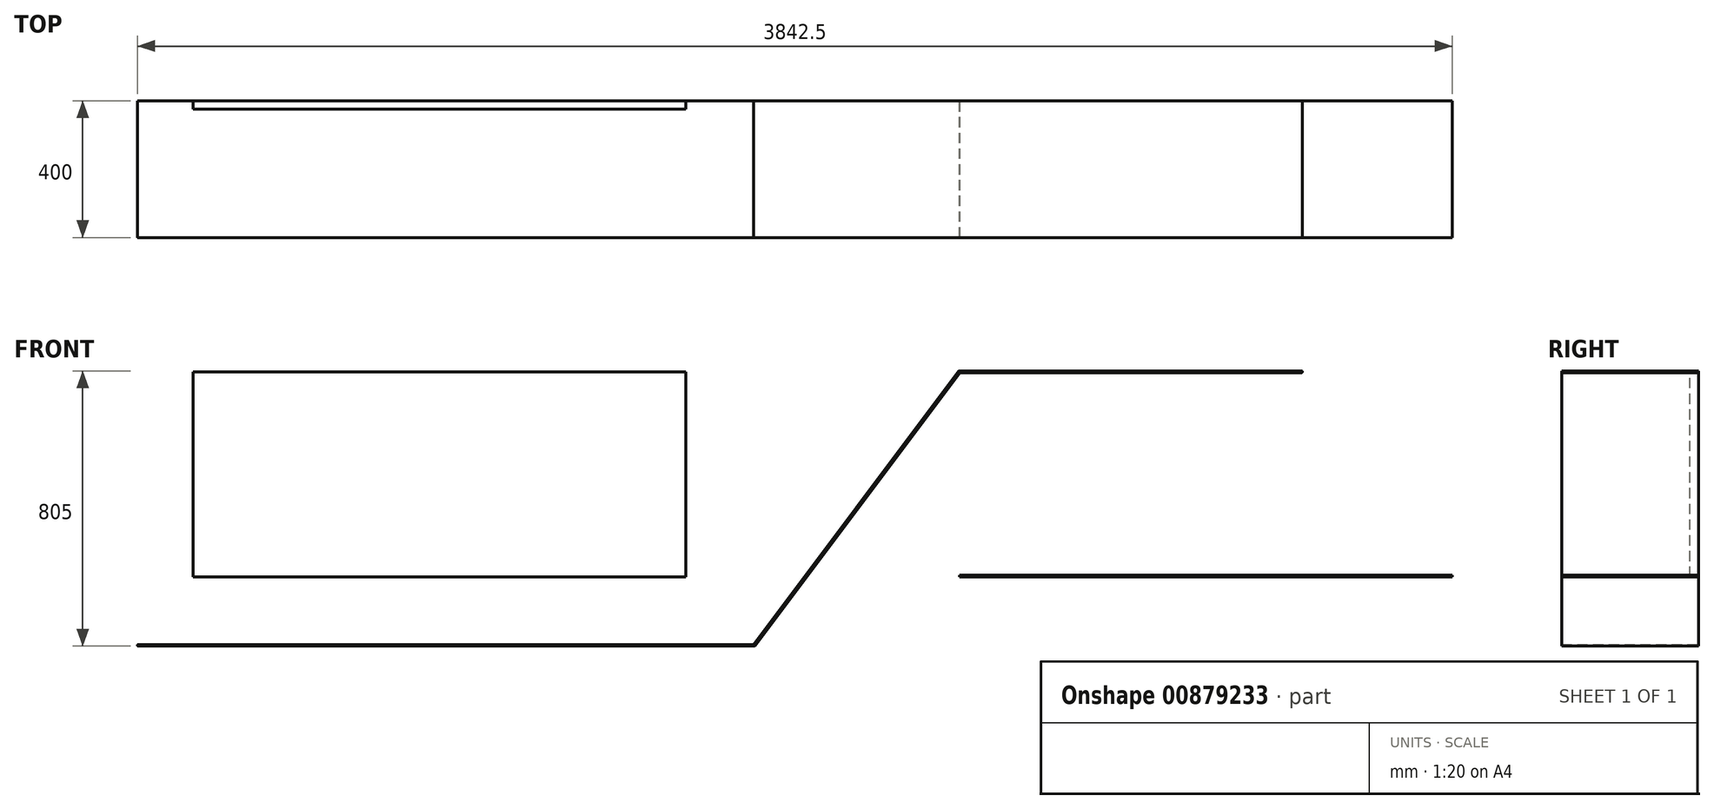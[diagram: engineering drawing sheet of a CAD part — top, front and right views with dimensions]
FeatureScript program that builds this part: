
annotation { "Feature Type Name" : "Feature", "Feature Type Description" : "" }
export const myFeature = defineFeature(function(context is Context, id is Id, definition is map)
    precondition{}
    {
        {
            var Q0;
            Q0=qCreatedBy(makeId("Front.planeOp"),FACE);
            var sketch = newSketch(context, id + "F0", { "sketchPlane" : qUnion([Q0])});
            skLineSegment(sketch, "E0.bottom", {"start": v(0, 0) * mm, "end": v(-1440, 0) * mm});
            skLineSegment(sketch, "E0.top", {"start": v(0, 600) * mm, "end": v(-1440, 600) * mm});
            skLineSegment(sketch, "E0.left", {"start": v(0, 0) * mm, "end": v(0, 600) * mm});
            skLineSegment(sketch, "E0.right", {"start": v(-1440, 0) * mm, "end": v(-1440, 600) * mm});
            skSolve(sketch);
        }
        {
            var Q0;
            Q0=makeQuery(id+"F0.imprint","IMPRINT",FACE,{"disambiguationData":[TD([[makeQuery(id+"F0.imprint","IMPRINT",EDGE,{"derivedFrom":sQuery(id+"F0.wireOp",EDGE,"E0.bottom")}),-1.0]])]});
            extrude(context, id + "F1", {"entities" : qUnion([Q0]), "depth" : 25 * mm, "offsetDistance" : 25 * mm});
        }
        {
            var Q0;
            Q0=qCreatedBy(makeId("Front.planeOp"),FACE);
            var sketch = newSketch(context, id + "F2", { "sketchPlane" : qUnion([Q0])});
            skLineSegment(sketch, "E1", {"start": v(-1600, -200) * mm, "end": v(200, -200) * mm});
            skLineSegment(sketch, "E2", {"start": v(200, -200) * mm, "end": v(800, 600) * mm});
            skLineSegment(sketch, "E3", {"start": v(800, 600) * mm, "end": v(1800, 600) * mm});
            skArc(sketch, "E4.0.startCap", {"start": v(-1600, -202.5) * mm, "mid": v(-1602.5, -200) * mm, "end": v(-1600, -197.5) * mm});
            skArc(sketch, "E4.0.endCap", {"start": v(200, -197.5) * mm, "mid": v(202.5, -200) * mm, "end": v(200, -202.5) * mm});
            skLineSegment(sketch, "E4.0.left", {"start": v(-1600, -197.5) * mm, "end": v(200, -197.5) * mm});
            skLineSegment(sketch, "E4.0.right", {"start": v(-1600, -202.5) * mm, "end": v(200, -202.5) * mm});
            skArc(sketch, "E4.1.startCap", {"start": v(202, -201.5) * mm, "mid": v(198.5, -202) * mm, "end": v(198, -198.5) * mm});
            skArc(sketch, "E4.1.endCap", {"start": v(798, 601.5) * mm, "mid": v(801.5, 602) * mm, "end": v(802, 598.5) * mm});
            skLineSegment(sketch, "E4.1.left", {"start": v(198, -198.5) * mm, "end": v(798, 601.5) * mm});
            skLineSegment(sketch, "E4.1.right", {"start": v(202, -201.5) * mm, "end": v(802, 598.5) * mm});
            skArc(sketch, "E4.2.startCap", {"start": v(800, 597.5) * mm, "mid": v(797.5, 600) * mm, "end": v(800, 602.5) * mm});
            skArc(sketch, "E4.2.endCap", {"start": v(1800, 602.5) * mm, "mid": v(1802.5, 600) * mm, "end": v(1800, 597.5) * mm});
            skLineSegment(sketch, "E4.2.left", {"start": v(800, 602.5) * mm, "end": v(1800, 602.5) * mm});
            skLineSegment(sketch, "E4.2.right", {"start": v(800, 597.5) * mm, "end": v(1800, 597.5) * mm});
            skLineSegment(sketch, "E5", {"start": v(800, 0) * mm, "end": v(2240, 0) * mm});
            skLineSegment(sketch, "E6", {"start": v(800, 0) * mm, "end": v(800, 5) * mm});
            skLineSegment(sketch, "E7", {"start": v(800, 5) * mm, "end": v(2240, 5) * mm});
            skLineSegment(sketch, "E8", {"start": v(2240, 0) * mm, "end": v(2240, 5) * mm});
            skSolve(sketch);
        }
        {
            var Q0;
            Q0 = qSketchRegion(id + "F2", true);
            extrude(context, id + "F3", {"entities" : qUnion([Q0]), "depth" : 400 * mm, "offsetDistance" : 25 * mm});
        }
    });
